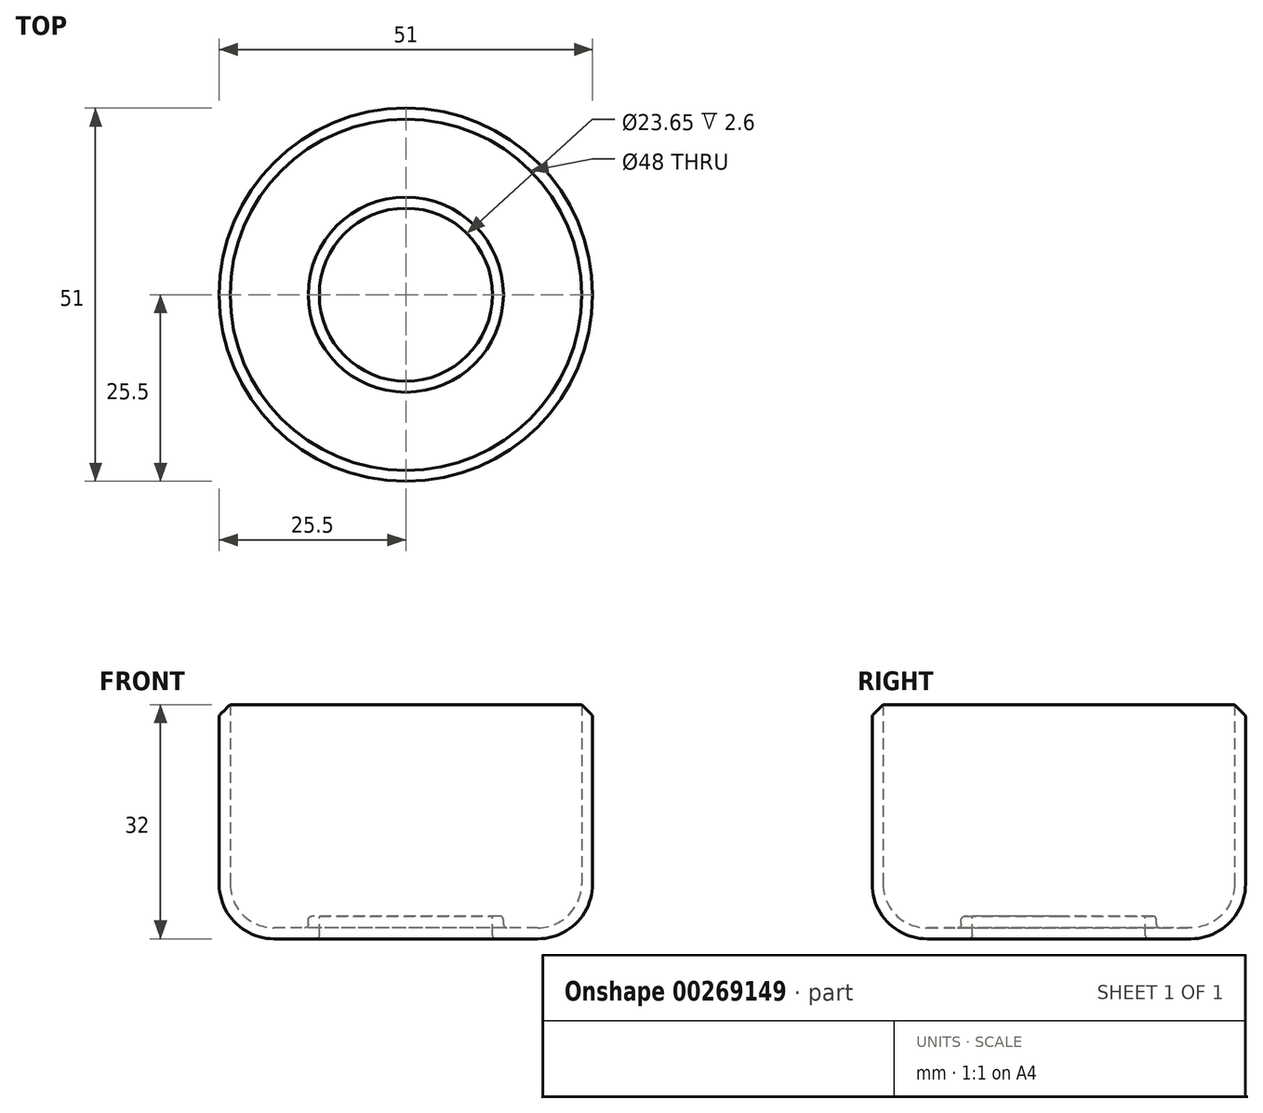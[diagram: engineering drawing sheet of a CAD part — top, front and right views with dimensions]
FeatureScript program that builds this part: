
annotation { "Feature Type Name" : "Feature", "Feature Type Description" : "" }
export const myFeature = defineFeature(function(context is Context, id is Id, definition is map)
    precondition{}
    {
        {
            var Q0;
            Q0=qCreatedBy(makeId("Front.planeOp"),FACE);
            var sketch = newSketch(context, id + "F0", { "sketchPlane" : qUnion([Q0]), "disableImprinting" : false});
            skLineSegment(sketch, "E0", {"start": v(0, 0) * mm, "end": v(0, -15.48) * mm, "construction": true});
            skPoint(sketch, "E1", {"position": v(0, -4.4) * mm});
            skLineSegment(sketch, "E2", {"start": v(18, -6) * mm, "end": v(14.71, -6) * mm});
            skPoint(sketch, "E3", {"position": v(0, 0) * mm});
            skPoint(sketch, "E4", {"position": v(20.13, -6) * mm});
            skLineSegment(sketch, "E5", {"start": v(24, 0) * mm, "end": v(24, 0) * mm});
            skPoint(sketch, "E6.visualSharp", {"position": v(24, -6) * mm});
            skArc(sketch, "E6.filletArc", {"start": v(18, -6) * mm, "mid": v(22.24, -4.24) * mm, "end": v(24, 0) * mm});
            skLineSegment(sketch, "E7", {"start": v(13.86, -4.4) * mm, "end": v(0, -4.4) * mm});
            skLineSegment(sketch, "E8", {"start": v(0, 0) * mm, "end": v(24, 0) * mm});
            skLineSegment(sketch, "E9", {"start": v(0, -4.4) * mm, "end": v(0, 0) * mm});
            skLineSegment(sketch, "E10", {"start": v(14.71, -6) * mm, "end": v(13.82, -6) * mm});
            skLineSegment(sketch, "E11", {"start": v(13.32, -5.5) * mm, "end": v(13.32, -4.9) * mm});
            skLineSegment(sketch, "E12", {"start": v(13.86, -4.4) * mm, "end": v(12.82, -4.4) * mm});
            skPoint(sketch, "E13.visualSharp", {"position": v(13.32, -6) * mm});
            skArc(sketch, "E13.filletArc", {"start": v(13.32, -5.5) * mm, "mid": v(13.47, -5.85) * mm, "end": v(13.82, -6) * mm});
            skPoint(sketch, "E14.visualSharp", {"position": v(13.32, -4.4) * mm});
            skArc(sketch, "E14.filletArc", {"start": v(13.32, -4.9) * mm, "mid": v(13.18, -4.55) * mm, "end": v(12.82, -4.4) * mm});
            skSolve(sketch);
        }
        {
            var Q0;
            Q0=qCreatedBy(makeId("Front.planeOp"),FACE);
            var sketch = newSketch(context, id + "F1", { "sketchPlane" : qUnion([Q0]), "disableImprinting" : false});
            skLineSegment(sketch, "E15.0", {"start": v(0, 0) * mm, "end": v(24, 0) * mm, "construction": true});
            skLineSegment(sketch, "E16", {"start": v(24, 0) * mm, "end": v(25.5, 0) * mm});
            skArc(sketch, "E17.0", {"start": v(18, -7.5) * mm, "mid": v(23.3, -5.3) * mm, "end": v(25.5, 0) * mm});
            skLineSegment(sketch, "E17.1", {"start": v(11.82, -7) * mm, "end": v(11.82, -4.9) * mm});
            skLineSegment(sketch, "E17.4", {"start": v(18, -7.5) * mm, "end": v(12.32, -7.5) * mm});
            skLineSegment(sketch, "E18", {"start": v(11.82, -4.9) * mm, "end": v(11.82, 0) * mm});
            skLineSegment(sketch, "E19", {"start": v(11.82, 0) * mm, "end": v(24, 0) * mm});
            skPoint(sketch, "E20.visualSharp", {"position": v(11.82, -7.5) * mm});
            skArc(sketch, "E20.filletArc", {"start": v(11.82, -7) * mm, "mid": v(11.97, -7.35) * mm, "end": v(12.32, -7.5) * mm});
            skLineSegment(sketch, "E21", {"start": v(25.5, 0) * mm, "end": v(25.5, 25) * mm});
            skLineSegment(sketch, "E22", {"start": v(25.5, 25) * mm, "end": v(11.82, 25) * mm});
            skLineSegment(sketch, "E23", {"start": v(11.82, 25) * mm, "end": v(11.82, 0) * mm});
            skSolve(sketch);
        }
        {
            var Q0;
            Q0=makeQuery(id+"F0.imprint","IMPRINT",FACE,{"disambiguationData":[TD([[makeQuery(id+"F0.imprint","IMPRINT",EDGE,{"derivedFrom":sQuery(id+"F0.wireOp",EDGE,"E2")}),-1.0]])]});
            var Q1;
            Q1=sQuery(id+"F0.wireOp",EDGE,"E0");
            revolve(context, id + "F2", {"surfaceOperationType" : NewSurfaceOperationType.NEW, "entities" : qUnion([Q0]), "axis" : qUnion([Q1]), "revolveType" : RevolveType.FULL});
        }
        {
            var Q0;
            Q0=makeQuery(id+"F2.opRevolve","SWEPT_FACE",FACE,{"disambiguationData":[OSD([sQuery(id+"F0.wireOp",EDGE,"E8")])]});
            extrude(context, id + "F3", {"entities" : qUnion([Q0]), "operationType" : NewBodyOperationType.ADD, "depth" : 45 * mm, "offsetDistance" : 25 * mm});
        }
        {
            var Q0;
            Q0 = qSketchRegion(id + "F1", true);
            var Q1;
            Q1=sQuery(id+"F0.wireOp",EDGE,"E0");
            revolve(context, id + "F4", {"surfaceOperationType" : NewSurfaceOperationType.NEW, "entities" : qUnion([Q0]), "axis" : qUnion([Q1]), "revolveType" : RevolveType.FULL});
        }
        {
            var Q0;
            Q0=makeQuery(id+"F2.opRevolve","SWEPT_BODY",BODY,{"disambiguationData":[OSD([sQuery(id+"F0.wireOp",EDGE,"E2"),sQuery(id+"F0.wireOp",EDGE,"E6.filletArc"),sQuery(id+"F0.wireOp",EDGE,"E7"),sQuery(id+"F0.wireOp",EDGE,"E8"),sQuery(id+"F0.wireOp",EDGE,"E9"),sQuery(id+"F0.wireOp",EDGE,"E10"),sQuery(id+"F0.wireOp",EDGE,"E11"),sQuery(id+"F0.wireOp",EDGE,"E13.filletArc"),sQuery(id+"F0.wireOp",EDGE,"E14.filletArc")])]});
            var Q1;
            Q1=makeQuery(id+"F4.opRevolve","SWEPT_BODY",BODY,{"disambiguationData":[OSD([sQuery(id+"F1.wireOp",EDGE,"E16"),sQuery(id+"F1.wireOp",EDGE,"E17.0"),sQuery(id+"F1.wireOp",EDGE,"E17.1"),sQuery(id+"F1.wireOp",EDGE,"E17.2"),sQuery(id+"F1.wireOp",EDGE,"E17.3"),sQuery(id+"F1.wireOp",EDGE,"E17.4"),sQuery(id+"F1.wireOp",EDGE,"E18"),sQuery(id+"F1.wireOp",EDGE,"E19")])]});
            booleanBodies(context, id + "F5", {"operationType" : BooleanOperationType.SUBTRACTION, "tools" : qUnion([Q0]), "targets" : qUnion([Q1])});
        }
        {
            var Q0;
            Q0=makeQuery(id+"F4.opRevolve","SWEPT_EDGE",EDGE,{"disambiguationData":[OSD([sQuery(id+"F1.wireOp",EDGE,"E21"),sQuery(id+"F1.wireOp",EDGE,"E22")])]});
            chamfer(context, id + "F6", {"entities" : qUnion([Q0]), "width" : 2 * mm, "tangentPropagation" : true});
        }
        {
            var Q0;
            {var subQ0=sQuery(id+"F1.wireOp",EDGE,"E21");Q0=makeQuery(id+"F6.opChamfer","BLEND_EDGE",EDGE,{"blendedFrom":[makeQuery(id+"F4.opRevolve","SWEPT_EDGE",EDGE,{"disambiguationData":[OSD([subQ0,sQuery(id+"F1.wireOp",EDGE,"E22")])]}),makeQuery(id+"F4.opRevolve","SWEPT_FACE",FACE,{"disambiguationData":[OSD([subQ0])]})],"blendedInto":[makeQuery(id+"F4.opRevolve","SWEPT_FACE",FACE,{"disambiguationData":[OSD([subQ0])]})]});}
            fillet(context, id + "F7", {"entities" : qUnion([Q0]), "tangentPropagation" : true, "radius" : 0.5 * mm, "defaultsChanged" : false, "vertexSettings" : [], "allowEdgeOverflow" : false});
        }
    });
